# Revit family: FoodserviceScheduleMaker
name_source: partatom
category: Specialty Equipment
revit_build: Autodesk Revit 2017 (Build: 20181011_1645(x64)
units: mm (PartAtom-declared; Revit-internal decimal feet)

## family parameters
Always vertical = Yes
Cut with Voids When Loaded = No
Part Type = Normal
Room Calculation Point = No
Round Connector Dimension = Use Diameter
Shared = No
Work Plane-Based = No

## types (1)
- FoodserviceScheduleMaker
    Apparent Power = 12440 VA
    BTUH = 1.0 Btu/h
    CO2 Connection Height = 1' - 0"
    CO2 Pressure = 1.00 psi
    CO2 RI Height = 1' - 0"
    CO2 Size = 1"
    CO2 Volume = 1 GPM
    Chilled Water Flow = 1 GPM
    Chilled Water Maximum Pressure = 1.00 psi
    Chilled Water Minimum Pressure = 1.00 psi
    Chilled Water Return Connection Height = 1' - 0"
    Chilled Water Return RI Height = 1' - 0"
    Chilled Water Return Size = 1"
    Chilled Water Supply Connection Height = 1' - 0"
    Chilled Water Supply RI Height = 1' - 0"
    Chilled Water Supply Size = 1"
    Chilled Water Temperature = 1 °F
    Cold Water Connection Height = 1' - 0"
    Cold Water Consumption = 12
    Cold Water Flow = 1 GPM
    Cold Water Maximum Pressure = 1.00 psi
    Cold Water Minimum Pressure = 1.00 psi
    Cold Water RI Height = 1' - 0"
    Cold Water Size = 1"
    Cold Water Temperature Recommended = 1 °F
    Compressed Air Connection Height = 1' - 0"
    Compressed Air Pressure = 1.00 psi
    Compressed Air RI Height = 1' - 0"
    Compressed Air Size = 1"
    Compressed Air Volume = 1 GPM
    Condensate Return Connection Height = 1' - 0"
    Condensate Return RI Height = 1' - 0"
    Condensate Return Size = 1"
    Conn Conduit = Yes
    Conn Plug = NEMA 5-15P
    Cycle = 60 Hz
    Direct Waste Connection Height = 1' - 0"
    Direct Waste Flow = 1 GPM
    Direct Waste RI Height = 1' - 0"
    Direct Waste Size = 1"
    Elec Conn Connection Height = 2' - 0"
    Elec Conn RI Height = 1' - 0"
    Electric Connection Type = Direct
    Exhaust RI Height = 1' - 0"
    Exhaust Static Press = 1.00 in-wg
    Exhaust Vent Depth = 1' - 0"
    Exhaust Vent Diameter = 1' - 0"
    Exhaust Vent Width = 1' - 0"
    Exhaust Volume = 1 CFM
    FL Amps = 13 A
    Filtered Water Connection Height = 1' - 0"
    Filtered Water Flow = 1 GPM
    Filtered Water RI Height = 1' - 0"
    Filtered Water Supply Size = 1"
    Foodservice Equipment Identifier = Yes
    Gas Connection Height = 1' - 0"
    Gas Input = 1.0 Btu/h
    Gas KW = 1
    Gas RI Height = 1' - 0"
    Gas Size = 1"
    Hot Water Connection Height = 1' - 0"
    Hot Water Consumption = 1 GPM
    Hot Water Flow = 1 GPM
    Hot Water Maximum Pressure = 1.00 psi
    Hot Water Minimum Pressure = 1.00 psi
    Hot Water RI Height = 1' - 0"
    Hot Water Size = 1"
    Hot Water Temperature = 1 °F
    Identify Quantity as Lot = Yes
    Indirect Waste Connection Height = 1' - 0"
    Indirect Waste Connection Type = (2) To Floor Sink
    Indirect Waste Flow = 1 GPM
    Indirect Waste Size = 1"
    KCL Exhaust Connection Height = 1' - 0"
    KCL Indirect Waste RI Height = 1' - 0"
    KCL MU Connection Height = 1' - 0"
    MU Air RI Height = 1' - 0"
    MU Air Static Press = 1.00 in-wg
    MU Air Vent Depth = 1' - 0"
    MU Air Vent Diameter = 1' - 0"
    MU Air Vent Width = 1' - 0"
    MU Air Volume = 1 CFM
    Max Overcurrent Protection = 20 A
    Min Ckt Ampacity = 20 A
    Number of Poles = 1
    Phase = 1
    Refrigerant Volume = 1.00 kip
    Steam Pounds per Hour = 1
    Steam Supply Connection Height = 1' - 0"
    Steam Supply Maximum Pressure = 1.00 psi
    Steam Supply Minimum Pressure = 1.00 psi
    Steam Supply RI Height = 1' - 0"
    Steam Supply Size = 1"
    Steam Supply Volume = 1 GPM
    Volts = 120 V
    Waste Water Discharge Temperature = 1 °F
    Watts = 12440 W
    Weight in Pounds = 0

## geometry (parser evidence)
native form markers: Sweep x2
no freeform markers — native parametric forms only
